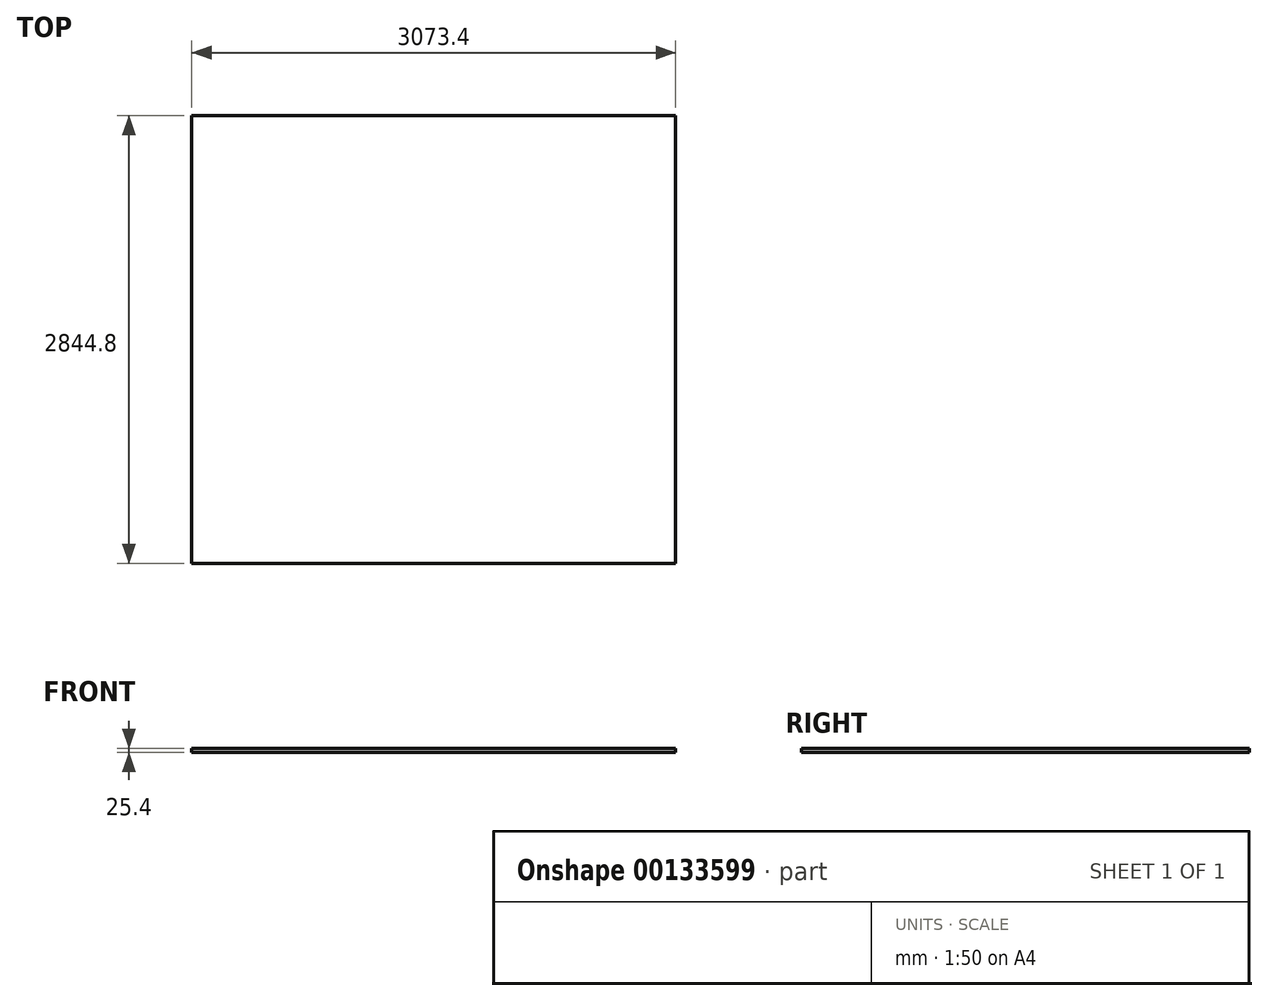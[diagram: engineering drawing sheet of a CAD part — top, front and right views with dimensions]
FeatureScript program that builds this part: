
annotation { "Feature Type Name" : "Feature", "Feature Type Description" : "" }
export const myFeature = defineFeature(function(context is Context, id is Id, definition is map)
    precondition{}
    {
        {
            var Q0;
            Q0=qCreatedBy(makeId("Top.planeOp"),FACE);
            var sketch = newSketch(context, id + "F0", { "sketchPlane" : qUnion([Q0])});
            skLineSegment(sketch, "E0.bottom", {"start": v(1536.7, -1422.4) * mm, "end": v(-1536.7, -1422.4) * mm});
            skLineSegment(sketch, "E0.top", {"start": v(1536.7, 1422.4) * mm, "end": v(-1536.7, 1422.4) * mm});
            skLineSegment(sketch, "E0.left", {"start": v(1536.7, -1422.4) * mm, "end": v(1536.7, 1422.4) * mm});
            skLineSegment(sketch, "E0.right", {"start": v(-1536.7, -1422.4) * mm, "end": v(-1536.7, 1422.4) * mm});
            skPoint(sketch, "E0.middle", {"position": v(0, 0) * mm});
            skSolve(sketch);
        }
        {
            var Q0;
            Q0=makeQuery(id+"F0.imprint","IMPRINT",FACE,{"disambiguationData":[TD([[makeQuery(id+"F0.imprint","IMPRINT",EDGE,{"derivedFrom":sQuery(id+"F0.wireOp",EDGE,"E0.bottom")}),-1.0]])]});
            extrude(context, id + "F1", {"entities" : qUnion([Q0]), "oppositeDirection" : true, "depth" : 25.4 * mm});
        }
    });
